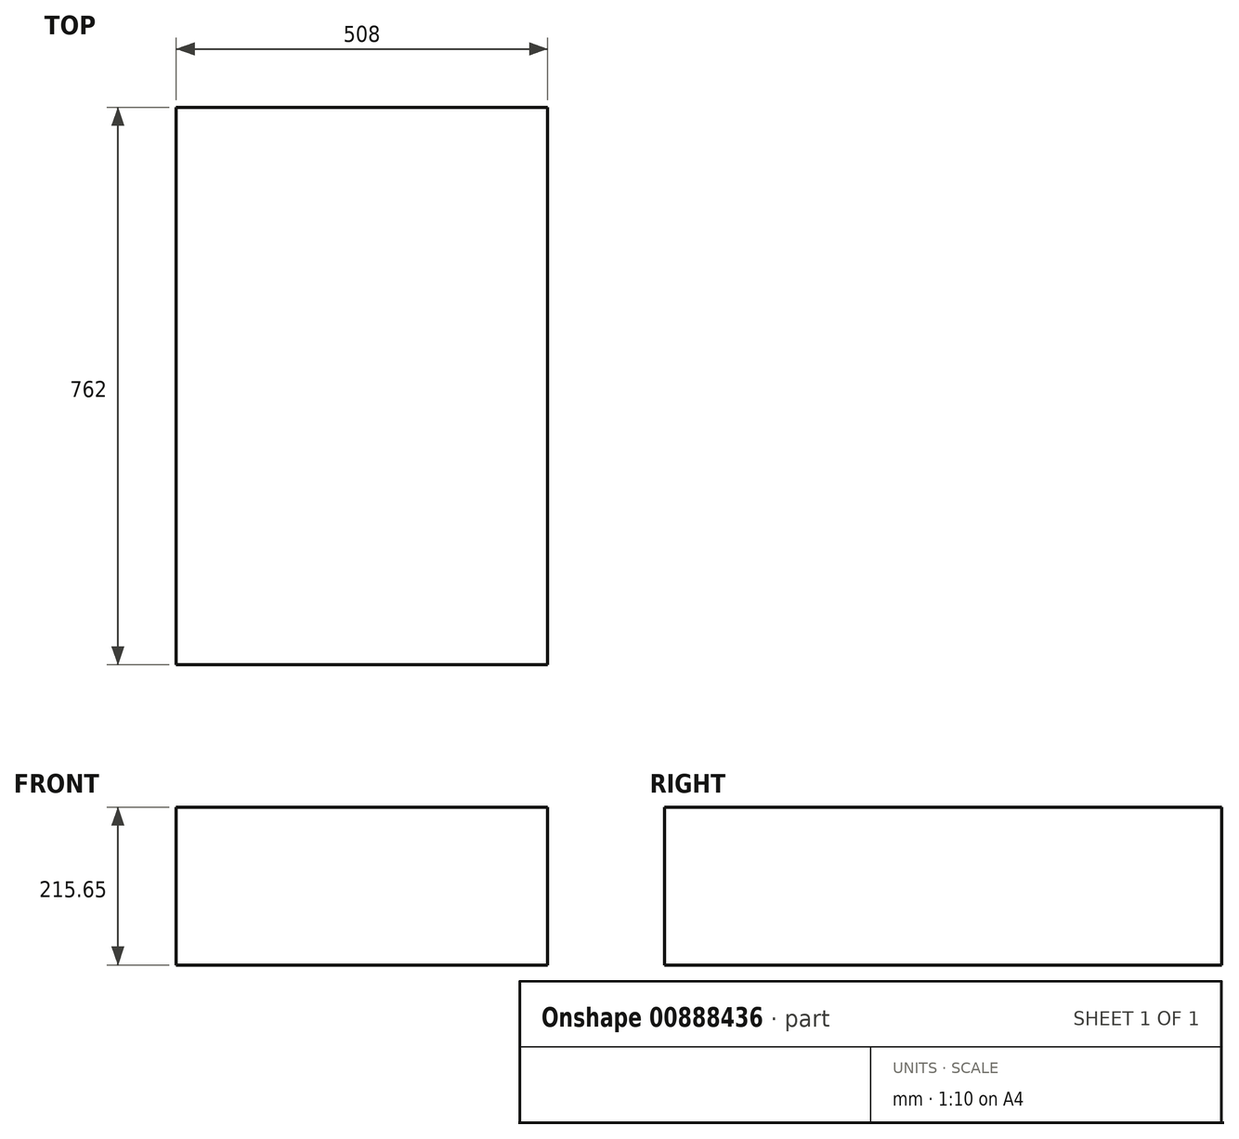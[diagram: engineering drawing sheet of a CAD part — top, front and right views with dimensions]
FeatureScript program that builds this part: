
annotation { "Feature Type Name" : "Feature", "Feature Type Description" : "" }
export const myFeature = defineFeature(function(context is Context, id is Id, definition is map)
    precondition{}
    {
        {
            var Q0;
            Q0=qCreatedBy(makeId("Top.planeOp"),FACE);
            var sketch = newSketch(context, id + "F0", { "sketchPlane" : qUnion([Q0])});
            skLineSegment(sketch, "E0.bottom", {"start": v(254, -381) * mm, "end": v(-254, -381) * mm});
            skLineSegment(sketch, "E0.top", {"start": v(254, 381) * mm, "end": v(-254, 381) * mm});
            skLineSegment(sketch, "E0.left", {"start": v(254, -381) * mm, "end": v(254, 381) * mm});
            skLineSegment(sketch, "E0.right", {"start": v(-254, -381) * mm, "end": v(-254, 381) * mm});
            skPoint(sketch, "E0.middle", {"position": v(0, 0) * mm});
            skSolve(sketch);
        }
        {
            var Q0;
            Q0 = qSketchRegion(id + "F0", true);
            extrude(context, id + "F1", {"entities" : qUnion([Q0]), "depth" : 215.65 * mm, "offsetDistance" : 25.4 * mm});
        }
    });
